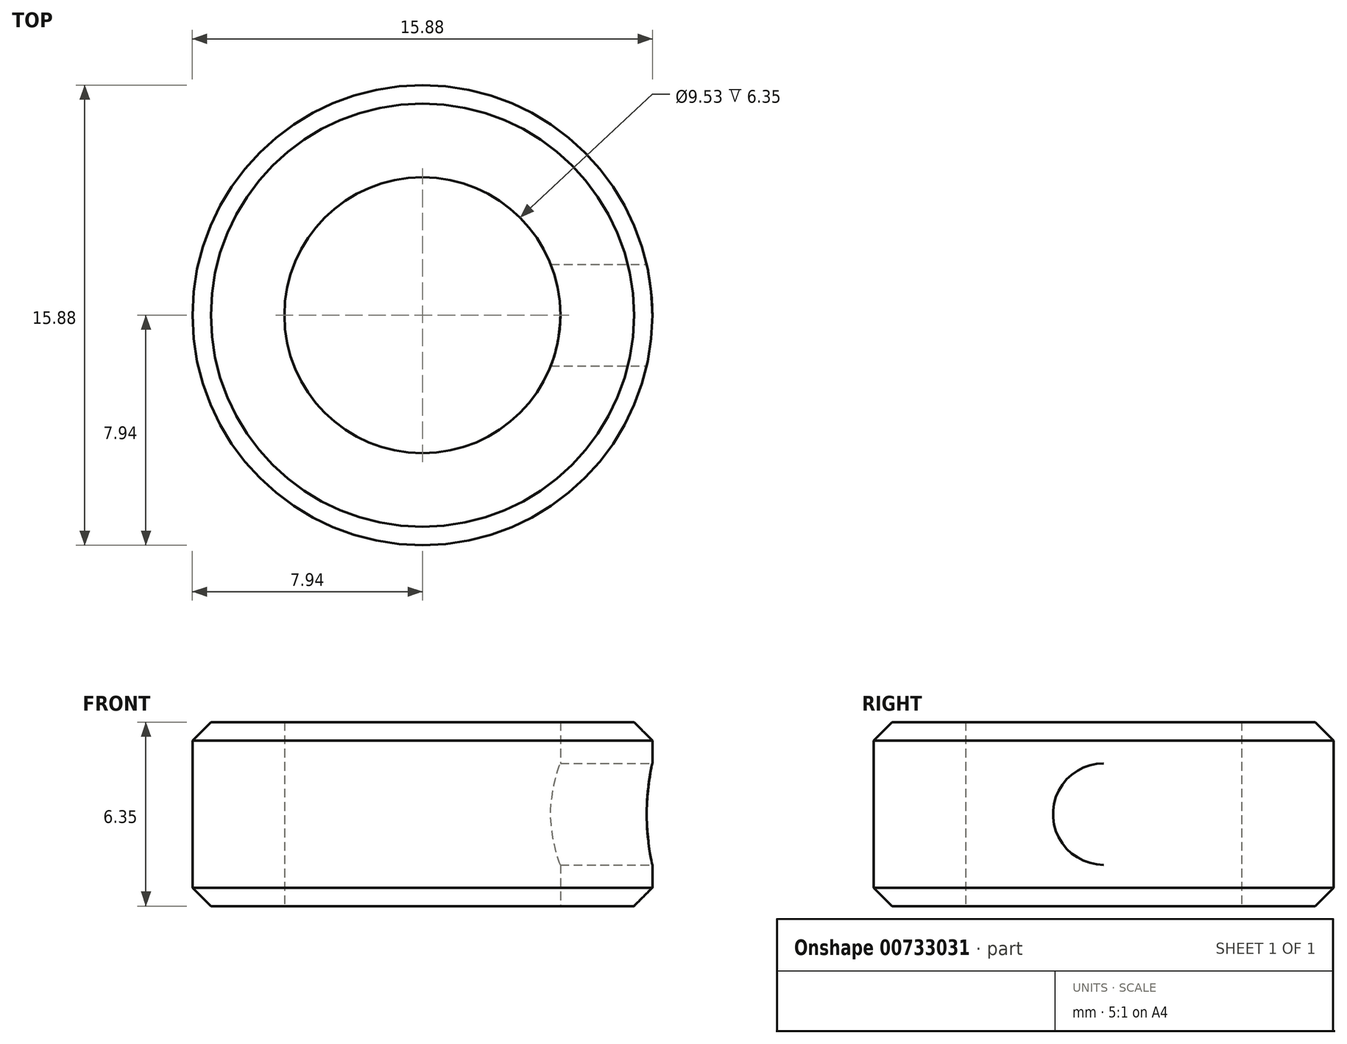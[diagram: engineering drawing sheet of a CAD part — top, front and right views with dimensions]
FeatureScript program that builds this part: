
annotation { "Feature Type Name" : "Feature", "Feature Type Description" : "" }
export const myFeature = defineFeature(function(context is Context, id is Id, definition is map)
    precondition{}
    {
        {
            var Q0;
            Q0=qCreatedBy(makeId("Top.planeOp"),FACE);
            var sketch = newSketch(context, id + "F0", { "sketchPlane" : qUnion([Q0])});
            skCircle(sketch, "E0", {"center": v(0, 0) * mm, "radius": 4.76 * mm});
            skCircle(sketch, "E1", {"center": v(0, 0) * mm, "radius": 7.94 * mm});
            skSolve(sketch);
        }
        {
            var Q0;
            Q0=makeQuery(id+"F0.imprint","IMPRINT",FACE,{"disambiguationData":[TD([[makeQuery(id+"F0.imprint","IMPRINT",EDGE,{"derivedFrom":sQuery(id+"F0.wireOp",EDGE,"E0")}),-1.0]])]});
            extrude(context, id + "F1", {"entities" : qUnion([Q0]), "depth" : 6.35 * mm, "offsetDistance" : 25.4 * mm});
        }
        {
            var Q0;
            Q0=qCreatedBy(makeId("Right.planeOp"),FACE);
            cPlane(context, id + "F2", {"entities" : qUnion([Q0]), "cplaneType" : CPlaneType.OFFSET, "offset" : 7.94 * mm, "width" : 152.4 * mm, "height" : 152.4 * mm});
        }
        {
            var Q0;
            Q0=qCreatedBy(id+"F2.planeOp",FACE);
            var sketch = newSketch(context, id + "F3", { "sketchPlane" : qUnion([Q0])});
            skCircle(sketch, "E2", {"center": v(0, 3.18) * mm, "radius": 1.75 * mm});
            skSolve(sketch);
        }
        {
            var Q0;
            Q0 = qSketchRegion(id + "F3", true);
            extrude(context, id + "F4", {"entities" : qUnion([Q0]), "operationType" : NewBodyOperationType.REMOVE, "oppositeDirection" : true, "depth" : 5.08 * mm, "offsetDistance" : 25.4 * mm});
        }
        {
            var Q0;
            Q0=makeQuery(id+"F1.opExtrude","CAP_EDGE",EDGE,{"disambiguationData":[OSD([sQuery(id+"F0.wireOp",EDGE,"E1")])],"isStart":false});
            var Q1;
            Q1=makeQuery(id+"F1.opExtrude","CAP_EDGE",EDGE,{"disambiguationData":[OSD([sQuery(id+"F0.wireOp",EDGE,"E1")])],"isStart":true});
            chamfer(context, id + "F5", {"entities" : qUnion([Q0, Q1]), "width" : 0.64 * mm, "tangentPropagation" : true});
        }
    });
